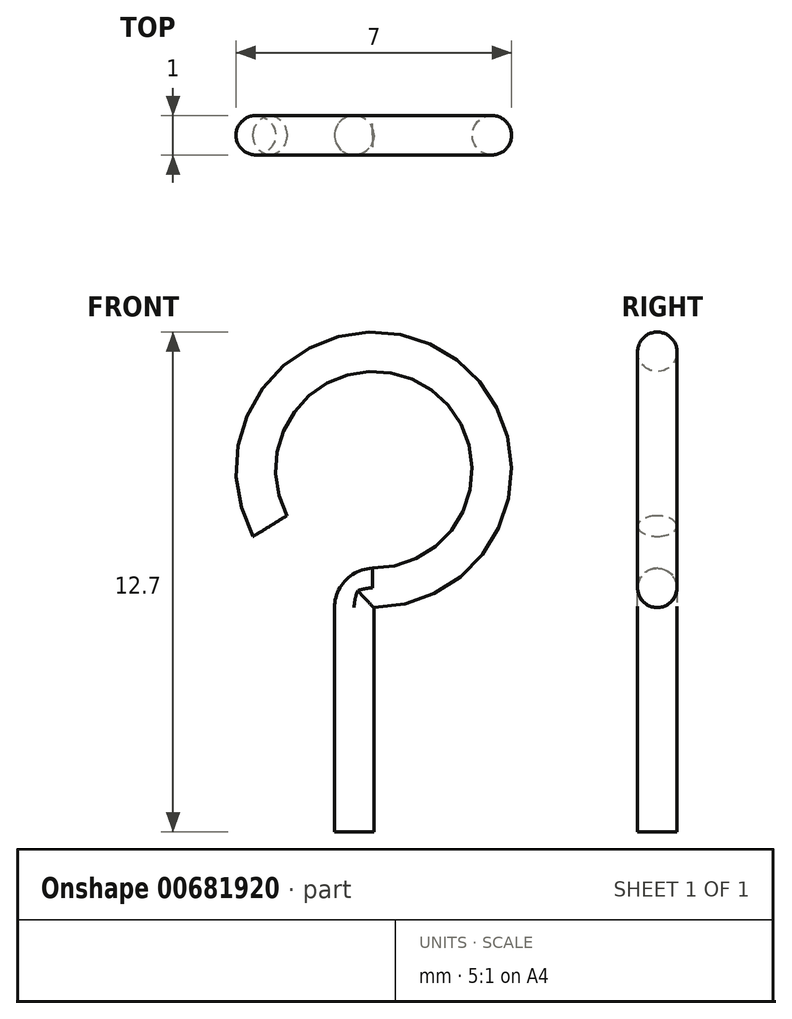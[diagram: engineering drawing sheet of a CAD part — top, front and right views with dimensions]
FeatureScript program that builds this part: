
annotation { "Feature Type Name" : "Feature", "Feature Type Description" : "" }
export const myFeature = defineFeature(function(context is Context, id is Id, definition is map)
    precondition{}
    {
        {
            var Q0;
            Q0=qCreatedBy(makeId("Front.planeOp"),FACE);
            var sketch = newSketch(context, id + "F0", { "sketchPlane" : qUnion([Q0])});
            skLineSegment(sketch, "E0", {"start": v(1, 2.13) * mm, "end": v(1, 6) * mm});
            skPoint(sketch, "E1", {"position": v(1, 13) * mm});
            skPoint(sketch, "E2", {"position": v(1, 9.5) * mm});
            skArc(sketch, "E3", {"start": v(1, 6) * mm, "mid": v(2.78, 12.51) * mm, "end": v(-2.06, 7.8) * mm});
            skArc(sketch, "E4.0", {"start": v(0.96, 7) * mm, "mid": v(2.3, 11.63) * mm, "end": v(-1.21, 8.33) * mm});
            skLineSegment(sketch, "E5", {"start": v(0, 2.13) * mm, "end": v(0, 6) * mm});
            skPoint(sketch, "E6", {"position": v(-2.06, 7.8) * mm});
            skLineSegment(sketch, "E7", {"start": v(-2.06, 7.8) * mm, "end": v(-1.21, 8.33) * mm});
            skPoint(sketch, "E8", {"position": v(0.96, 7) * mm});
            skArc(sketch, "E9", {"start": v(0.96, 7) * mm, "mid": v(0.28, 6.7) * mm, "end": v(0, 6) * mm});
            skPoint(sketch, "E10", {"position": v(1, 0.3) * mm});
            skLineSegment(sketch, "E11", {"start": v(1, 2.13) * mm, "end": v(1, 0.3) * mm});
            skLineSegment(sketch, "E12", {"start": v(0, 0.3) * mm, "end": v(0, 2.13) * mm});
            skLineSegment(sketch, "E13", {"start": v(0, 0.3) * mm, "end": v(1, 0.3) * mm});
            skSolve(sketch);
        }
        {
            var Q0;
            Q0=makeQuery(id+"F0.imprint","IMPRINT",FACE,{"disambiguationData":[TD([[makeQuery(id+"F0.imprint","IMPRINT",EDGE,{"derivedFrom":sQuery(id+"F0.wireOp",EDGE,"E0")}),1.0]])]});
            extrude(context, id + "F1", {"entities" : qUnion([Q0]), "oppositeDirection" : true, "depth" : 1 * mm, "offsetDistance" : 25.4 * mm});
        }
        {
            var Q0;
            Q0=makeQuery(id+"F1.opExtrude","CAP_EDGE",EDGE,{"disambiguationData":[OSD([sQuery(id+"F0.wireOp",EDGE,"E3")])],"isStart":true});
            var Q1;
            Q1=makeQuery(id+"F1.opExtrude","CAP_EDGE",EDGE,{"disambiguationData":[OSD([sQuery(id+"F0.wireOp",EDGE,"E3")])],"isStart":false});
            var Q2;
            Q2=makeQuery(id+"F1.opExtrude","CAP_EDGE",EDGE,{"disambiguationData":[OSD([sQuery(id+"F0.wireOp",EDGE,"E4.0")])],"isStart":true});
            var Q3;
            Q3=makeQuery(id+"F1.opExtrude","CAP_EDGE",EDGE,{"disambiguationData":[OSD([sQuery(id+"F0.wireOp",EDGE,"E0")])],"isStart":true});
            var Q4;
            Q4=makeQuery(id+"F1.opExtrude","CAP_EDGE",EDGE,{"disambiguationData":[OSD([sQuery(id+"F0.wireOp",EDGE,"E0")])],"isStart":false});
            var Q5;
            Q5=makeQuery(id+"F1.opExtrude","CAP_EDGE",EDGE,{"disambiguationData":[OSD([sQuery(id+"F0.wireOp",EDGE,"E5")])],"isStart":true});
            var Q6;
            Q6=makeQuery(id+"F1.opExtrude","CAP_EDGE",EDGE,{"disambiguationData":[OSD([sQuery(id+"F0.wireOp",EDGE,"E4.0")])],"isStart":false});
            var Q7;
            Q7=makeQuery(id+"F1.opExtrude","CAP_EDGE",EDGE,{"disambiguationData":[OSD([sQuery(id+"F0.wireOp",EDGE,"E9")])],"isStart":true});
            var Q8;
            Q8=makeQuery(id+"F1.opExtrude","CAP_EDGE",EDGE,{"disambiguationData":[OSD([sQuery(id+"F0.wireOp",EDGE,"E9")])],"isStart":false});
            fillet(context, id + "F2", {"entities" : qUnion([Q0, Q1, Q2, Q3, Q4, Q5, Q6, Q7, Q8]), "radius" : 0.5 * mm, "tangentPropagation" : true, "allowEdgeOverflow" : false});
        }
    });
